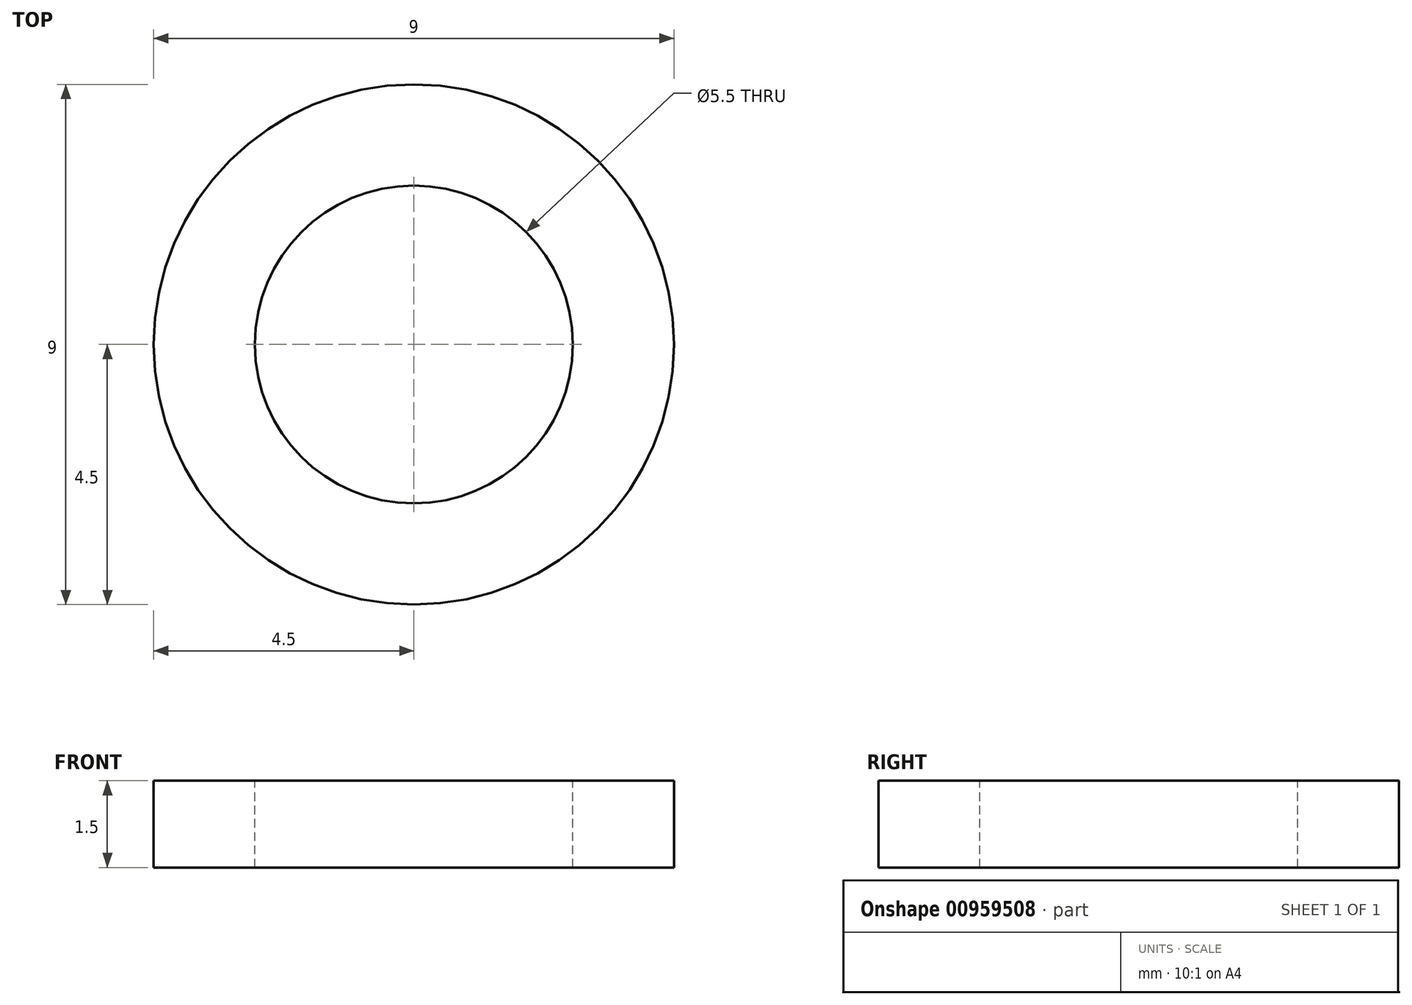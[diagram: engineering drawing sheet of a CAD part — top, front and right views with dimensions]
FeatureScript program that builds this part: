
annotation { "Feature Type Name" : "Feature", "Feature Type Description" : "" }
export const myFeature = defineFeature(function(context is Context, id is Id, definition is map)
    precondition{}
    {
        {
            var Q0;
            Q0=qCreatedBy(makeId("Top.planeOp"),FACE);
            var sketch = newSketch(context, id + "F0", { "sketchPlane" : qUnion([Q0])});
            skCircle(sketch, "E0", {"center": v(0, 0) * mm, "radius": 4.5 * mm});
            skSolve(sketch);
        }
        {
            var Q0;
            Q0=makeQuery(id+"F0.imprint","IMPRINT",FACE,{"disambiguationData":[TD([[makeQuery(id+"F0.imprint","IMPRINT",EDGE,{"derivedFrom":sQuery(id+"F0.wireOp",EDGE,"E0")}),1.0]])]});
            extrude(context, id + "F1", {"entities" : qUnion([Q0]), "depth" : 1.5 * mm, "offsetDistance" : 25 * mm});
        }
        {
            var Q0;
            Q0=sQuery(id+"F0.wireOp",VERTEX,"E0.center");
            var Q1;
            Q1=makeQuery(id+"F1.opExtrude","SWEPT_BODY",BODY,{"disambiguationData":[OSD([sQuery(id+"F0.wireOp",EDGE,"E0")])]});
            hole(context, id + "F2", {"style" : HoleStyle.SIMPLE, "endStyle" : HoleEndStyle.BLIND, "oppositeDirection" : true, "standardTappedOrClearance" : lookupTablePath({ "fit" : "Normal", "standard" : "ISO", "size" : "M5", "type" : "Clearance" }), "standardBlindInLast" : lookupTablePath({ "fit" : "Normal", "standard" : "ISO", "engagement" : "75%", "pitch" : "0.8 mm", "size" : "M5", "type" : "Clearance & tapped" }), "holeDiameter" : 5.5 * mm, "majorDiameter" : 5 * mm, "holeDepth" : 12 * mm, "tappedDepth" : 12 * mm, "tapClearance" : 3, "locations" : qUnion([Q0]), "scope" : qUnion([Q1]), "startStyle" : HoleStartStyle.PART});
        }
    });
